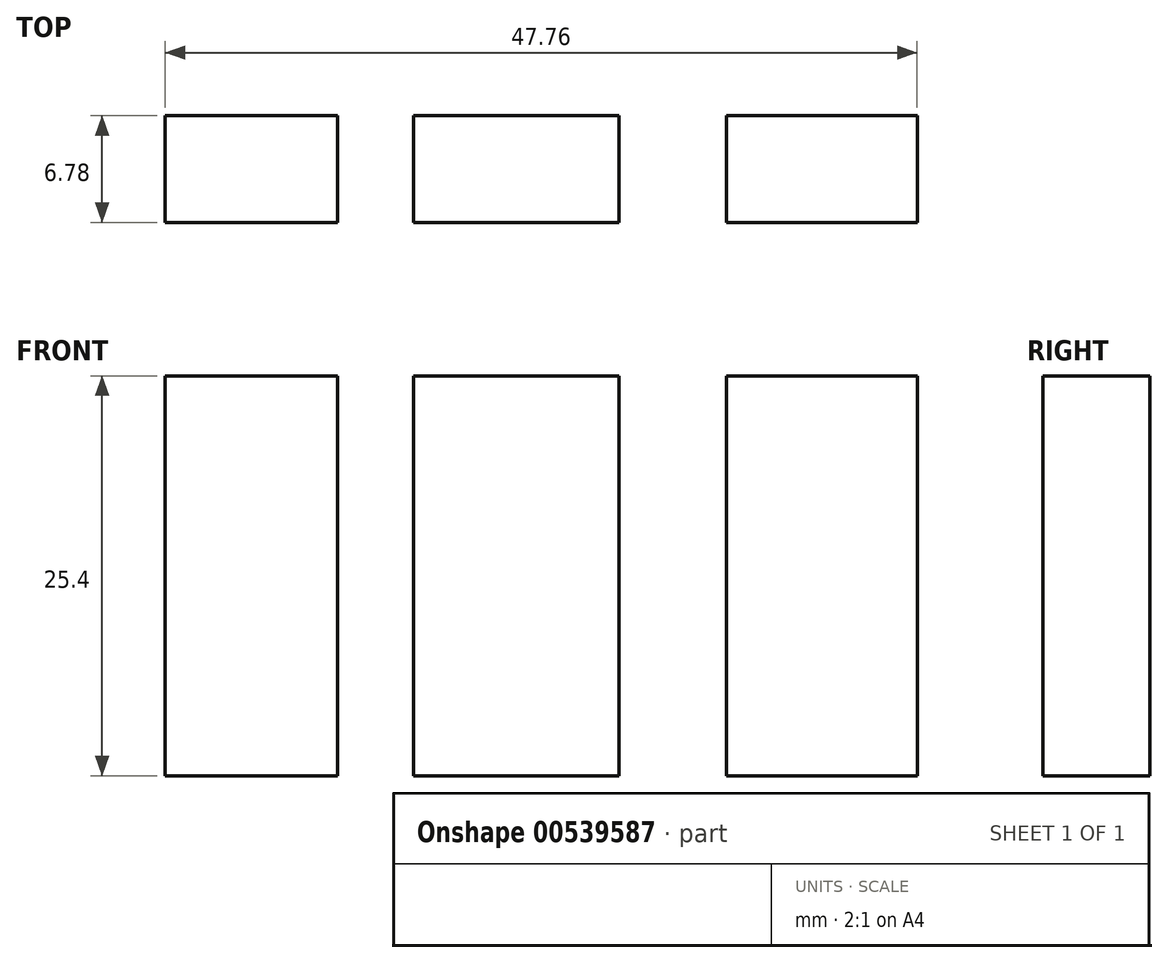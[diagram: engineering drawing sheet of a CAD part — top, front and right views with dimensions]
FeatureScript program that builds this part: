
annotation { "Feature Type Name" : "Feature", "Feature Type Description" : "" }
export const myFeature = defineFeature(function(context is Context, id is Id, definition is map)
    precondition{}
    {
        {
            var Q0;
            Q0=qCreatedBy(makeId("Top.planeOp"),FACE);
            var sketch = newSketch(context, id + "F0", { "sketchPlane" : qUnion([Q0])});
            skLineSegment(sketch, "E0.bottom", {"start": v(-77.11, 76.25) * mm, "end": v(76.5, 76.25) * mm});
            skLineSegment(sketch, "E0.top", {"start": v(-77.11, -76.61) * mm, "end": v(76.5, -76.61) * mm});
            skLineSegment(sketch, "E0.left", {"start": v(-77.11, 76.25) * mm, "end": v(-77.11, -76.61) * mm});
            skLineSegment(sketch, "E0.right", {"start": v(76.5, 76.25) * mm, "end": v(76.5, -76.61) * mm});
            skLineSegment(sketch, "E1.bottom", {"start": v(-88, 86.51) * mm, "end": v(89.96, 86.51) * mm});
            skLineSegment(sketch, "E1.top", {"start": v(-88, -87.04) * mm, "end": v(89.96, -87.04) * mm});
            skLineSegment(sketch, "E1.left", {"start": v(-88, 86.51) * mm, "end": v(-88, -87.04) * mm});
            skLineSegment(sketch, "E1.right", {"start": v(89.96, 86.51) * mm, "end": v(89.96, -87.04) * mm});
            skLineSegment(sketch, "E2.bottom", {"start": v(-70.28, 58.7) * mm, "end": v(-62.43, 58.7) * mm});
            skLineSegment(sketch, "E2.top", {"start": v(-70.28, 50.82) * mm, "end": v(-62.43, 50.82) * mm});
            skLineSegment(sketch, "E2.left", {"start": v(-70.28, 58.7) * mm, "end": v(-70.28, 50.82) * mm});
            skLineSegment(sketch, "E2.right", {"start": v(-62.43, 58.7) * mm, "end": v(-62.43, 50.82) * mm});
            skLineSegment(sketch, "E3.bottom", {"start": v(-56.42, 57.6) * mm, "end": v(-45.46, 57.6) * mm});
            skLineSegment(sketch, "E3.top", {"start": v(-56.42, 50.82) * mm, "end": v(-45.46, 50.82) * mm});
            skLineSegment(sketch, "E3.left", {"start": v(-56.42, 57.6) * mm, "end": v(-56.42, 50.82) * mm});
            skLineSegment(sketch, "E3.right", {"start": v(-45.46, 57.6) * mm, "end": v(-45.46, 50.82) * mm});
            skLineSegment(sketch, "E4.bottom", {"start": v(-40.64, 57.6) * mm, "end": v(-27.58, 57.6) * mm});
            skLineSegment(sketch, "E4.top", {"start": v(-40.64, 50.82) * mm, "end": v(-27.58, 50.82) * mm});
            skLineSegment(sketch, "E4.left", {"start": v(-40.64, 57.6) * mm, "end": v(-40.64, 50.82) * mm});
            skLineSegment(sketch, "E4.right", {"start": v(-27.58, 57.6) * mm, "end": v(-27.58, 50.82) * mm});
            skLineSegment(sketch, "E5.bottom", {"start": v(-27.58, 50.82) * mm, "end": v(-27.58, 50.82) * mm});
            skLineSegment(sketch, "E5.top", {"start": v(-27.58, 57.6) * mm, "end": v(-27.58, 57.6) * mm});
            skLineSegment(sketch, "E5.left", {"start": v(-27.58, 50.82) * mm, "end": v(-27.58, 57.6) * mm});
            skLineSegment(sketch, "E5.right", {"start": v(-27.58, 50.82) * mm, "end": v(-27.58, 57.6) * mm});
            skLineSegment(sketch, "E6.bottom", {"start": v(-20.78, 57.6) * mm, "end": v(-8.66, 57.6) * mm});
            skLineSegment(sketch, "E6.top", {"start": v(-20.78, 50.82) * mm, "end": v(-8.66, 50.82) * mm});
            skLineSegment(sketch, "E6.left", {"start": v(-20.78, 57.6) * mm, "end": v(-20.78, 50.82) * mm});
            skLineSegment(sketch, "E6.right", {"start": v(-8.66, 57.6) * mm, "end": v(-8.66, 50.82) * mm});
            skSolve(sketch);
        }
        {
            var Q0;
            Q0=makeQuery(id+"F0.imprint","IMPRINT",FACE,{"disambiguationData":[TD([[makeQuery(id+"F0.imprint","IMPRINT",EDGE,{"derivedFrom":sQuery(id+"F0.wireOp",EDGE,"E3.bottom")}),-1.0]])]});
            var Q1;
            Q1=makeQuery(id+"F0.imprint","IMPRINT",FACE,{"disambiguationData":[TD([[makeQuery(id+"F0.imprint","IMPRINT",EDGE,{"derivedFrom":sQuery(id+"F0.wireOp",EDGE,"E4.bottom")}),-1.0]])]});
            var Q2;
            Q2=makeQuery(id+"F0.imprint","IMPRINT",FACE,{"disambiguationData":[TD([[makeQuery(id+"F0.imprint","IMPRINT",EDGE,{"derivedFrom":sQuery(id+"F0.wireOp",EDGE,"E6.bottom")}),-1.0]])]});
            extrude(context, id + "F1", {"entities" : qUnion([Q0, Q1, Q2]), "depth" : 25.4 * mm, "offsetDistance" : 25.4 * mm});
        }
    });
